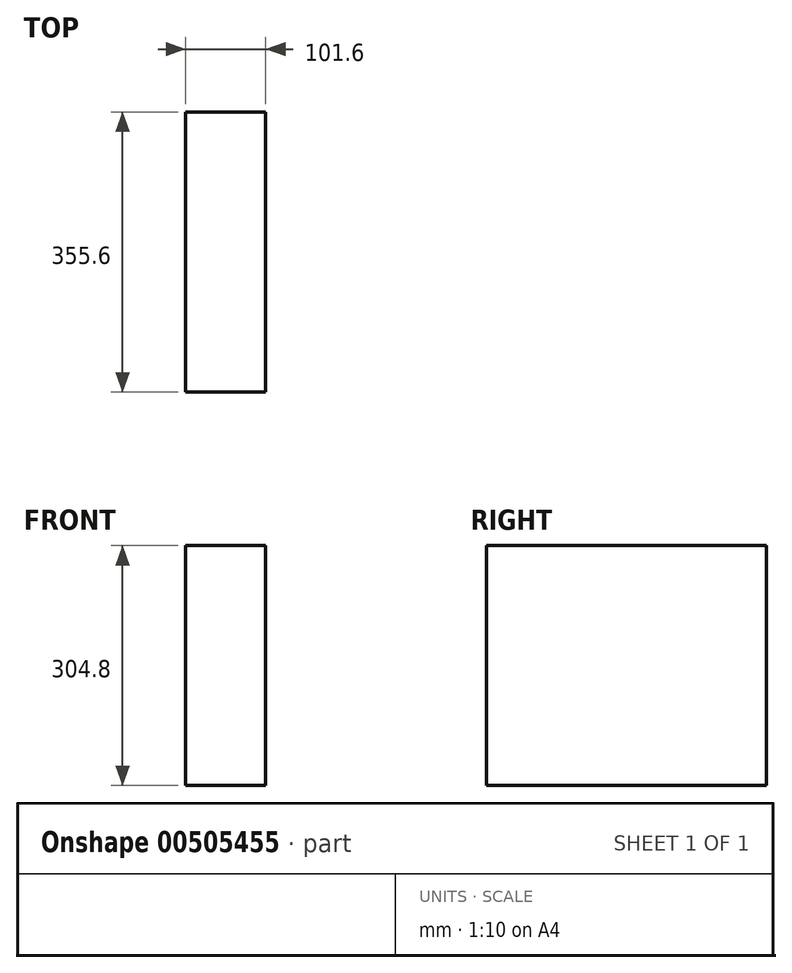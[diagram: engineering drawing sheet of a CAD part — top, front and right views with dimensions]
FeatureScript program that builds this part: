
annotation { "Feature Type Name" : "Feature", "Feature Type Description" : "" }
export const myFeature = defineFeature(function(context is Context, id is Id, definition is map)
    precondition{}
    {
        {
            var Q0;
            Q0=qCreatedBy(makeId("Front.planeOp"),FACE);
            var sketch = newSketch(context, id + "F0", { "sketchPlane" : qUnion([Q0])});
            skLineSegment(sketch, "E0.bottom", {"start": v(-53.57, 208.06) * mm, "end": v(48.03, 208.06) * mm});
            skLineSegment(sketch, "E0.top", {"start": v(-53.57, -96.74) * mm, "end": v(48.03, -96.74) * mm});
            skLineSegment(sketch, "E0.left", {"start": v(-53.57, 208.06) * mm, "end": v(-53.57, -96.74) * mm});
            skLineSegment(sketch, "E0.right", {"start": v(48.03, 208.06) * mm, "end": v(48.03, -96.74) * mm});
            skSolve(sketch);
        }
        {
            var Q0;
            Q0 = qSketchRegion(id + "F0", true);
            extrude(context, id + "F1", {"entities" : qUnion([Q0]), "depth" : 355.6 * mm});
        }
    });
